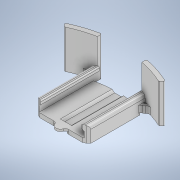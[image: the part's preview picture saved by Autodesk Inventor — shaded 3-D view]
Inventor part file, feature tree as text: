
AUTODESK INVENTOR PART (.ipt)
format: ipt  version: 2020 (Build 240168000, 168)  size: 853,504 bytes
history: native  units: mm
features: projected_geometry x17, other x10, sketch x10, extrude x9, fillet x2, chamfer x1
ambient origin geometry x8: Origin, YZ Plane, XZ Plane, XY Plane, X Axis, Y Axis, Z Axis, Center Point
bodies: Body1 (feature_tree)
feature tree (49):
  other  "Твердое тело1"
  sketch  "Эскиз1"
  other  "РабПлоскость4"
  sketch  "Эскиз2"
  other  "РабПлоскость5"
  sketch  "Эскиз3"
  other  "РабПлоскость6"
  sketch  "Эскиз4"
  other  "РабПлоскость7"
  sketch  "Эскиз5"
  other  "РабПлоскость8"
  sketch  "Эскиз6"
  extrude  "Выдавливание9"  TaperAngle=45.0deg  [1 undecoded]
  extrude  "Выдавливание10"  Depth=7.0mm
  other  "РабПлоскость1"
  extrude  "Выдавливание11"  Depth=20.0mm
  chamfer  "Фаска1"  Distance=7.0mm
  fillet  "Сопряжение1"  Radius=3.2mm
  fillet  "Сопряжение2"  Radius=59.0mm
  other  "РабПлоскость2"
  extrude  "Выдавливание12"  Depth=83.0mm
  other  "РабПлоскость9"
  sketch  "Эскиз9"
  extrude  "Выдавливание13"  Depth=69.0mm
  extrude  "Выдавливание14"  Depth=55.0mm
  other  "РабПлоскость3"
  extrude  "Выдавливание15"  Depth=3.0mm
  extrude  "Выдавливание16"  Depth=8.0mm
  extrude  "Выдавливание17"  Depth=5.0mm
  projected_geometry  "Спроецированная петля1"
  projected_geometry  "Спроецированная петля2"
  projected_geometry  "Спроецированная петля3"
  projected_geometry  "Спроецированная петля4"
  projected_geometry  "Спроецированная петля5"
  sketch  "Эскиз7"
  projected_geometry  "Спроецированная петля6"
  projected_geometry  "Спроецированная петля7"
  projected_geometry  "Спроецированная петля8"
  sketch  "Эскиз8"
  projected_geometry  "Спроецированная петля13"
  projected_geometry  "Спроецированная петля14"
  projected_geometry  "Спроецированная петля15"
  sketch  "Эскиз10"
  projected_geometry  "Спроецированная петля16"
  projected_geometry  "Спроецированная петля18"
  projected_geometry  "Спроецированная петля19"
  projected_geometry  "Спроецированная петля21"
  projected_geometry  "Спроецированная петля24"
  projected_geometry  "Спроецированная петля25"
note: 1 required parameter value undecoded (feature->parameter linkage not recoverable at this tier; creation-order binding heuristic only, values carry confidence <= 0.55)
